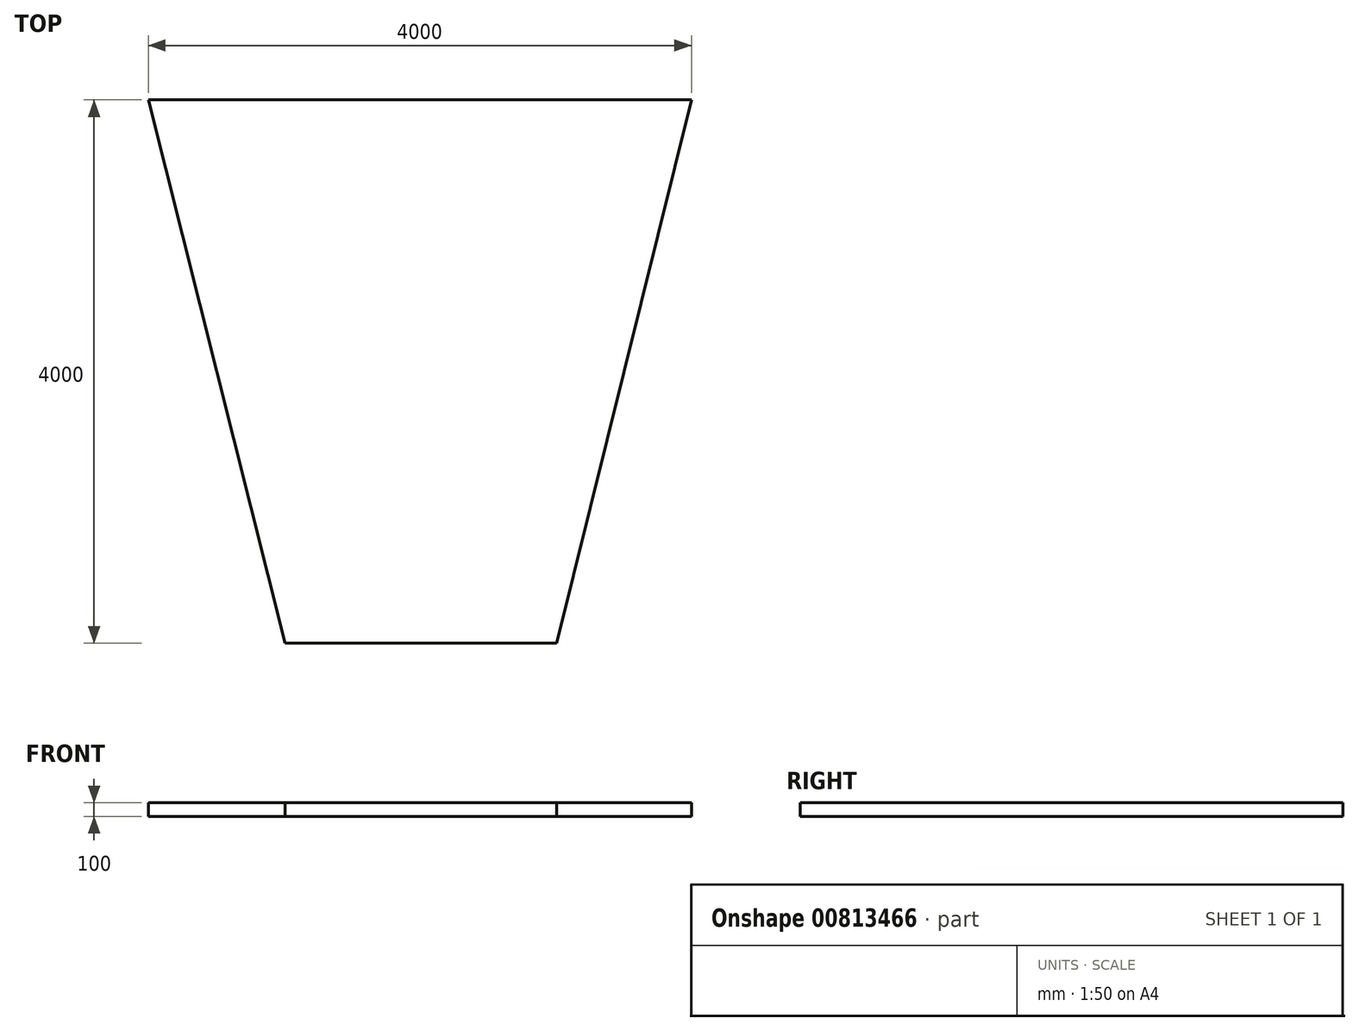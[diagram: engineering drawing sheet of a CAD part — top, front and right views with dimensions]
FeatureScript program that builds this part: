
annotation { "Feature Type Name" : "Feature", "Feature Type Description" : "" }
export const myFeature = defineFeature(function(context is Context, id is Id, definition is map)
    precondition{}
    {
        {
            var Q0;
            Q0=qCreatedBy(makeId("Top.planeOp"),FACE);
            var sketch = newSketch(context, id + "F0", { "sketchPlane" : qUnion([Q0])});
            skLineSegment(sketch, "E0", {"start": v(-2007.77, 34.29) * mm, "end": v(1992.23, 34.29) * mm});
            skLineSegment(sketch, "E1", {"start": v(-1000, -3965.71) * mm, "end": v(0, -3965.71) * mm});
            skLineSegment(sketch, "E2", {"start": v(-2007.77, 34.29) * mm, "end": v(-1000, -3965.71) * mm});
            skLineSegment(sketch, "E3.MirrorCS", {"start": v(1000, -3965.71) * mm, "end": v(0, -3965.71) * mm});
            skLineSegment(sketch, "E4", {"start": v(1992.23, 34.29) * mm, "end": v(1000, -3965.71) * mm});
            skSolve(sketch);
        }
        {
            var Q0;
            Q0 = qSketchRegion(id + "F0", true);
            extrude(context, id + "F1", {"entities" : qUnion([Q0]), "depth" : 100 * mm, "offsetDistance" : 25 * mm});
        }
    });
